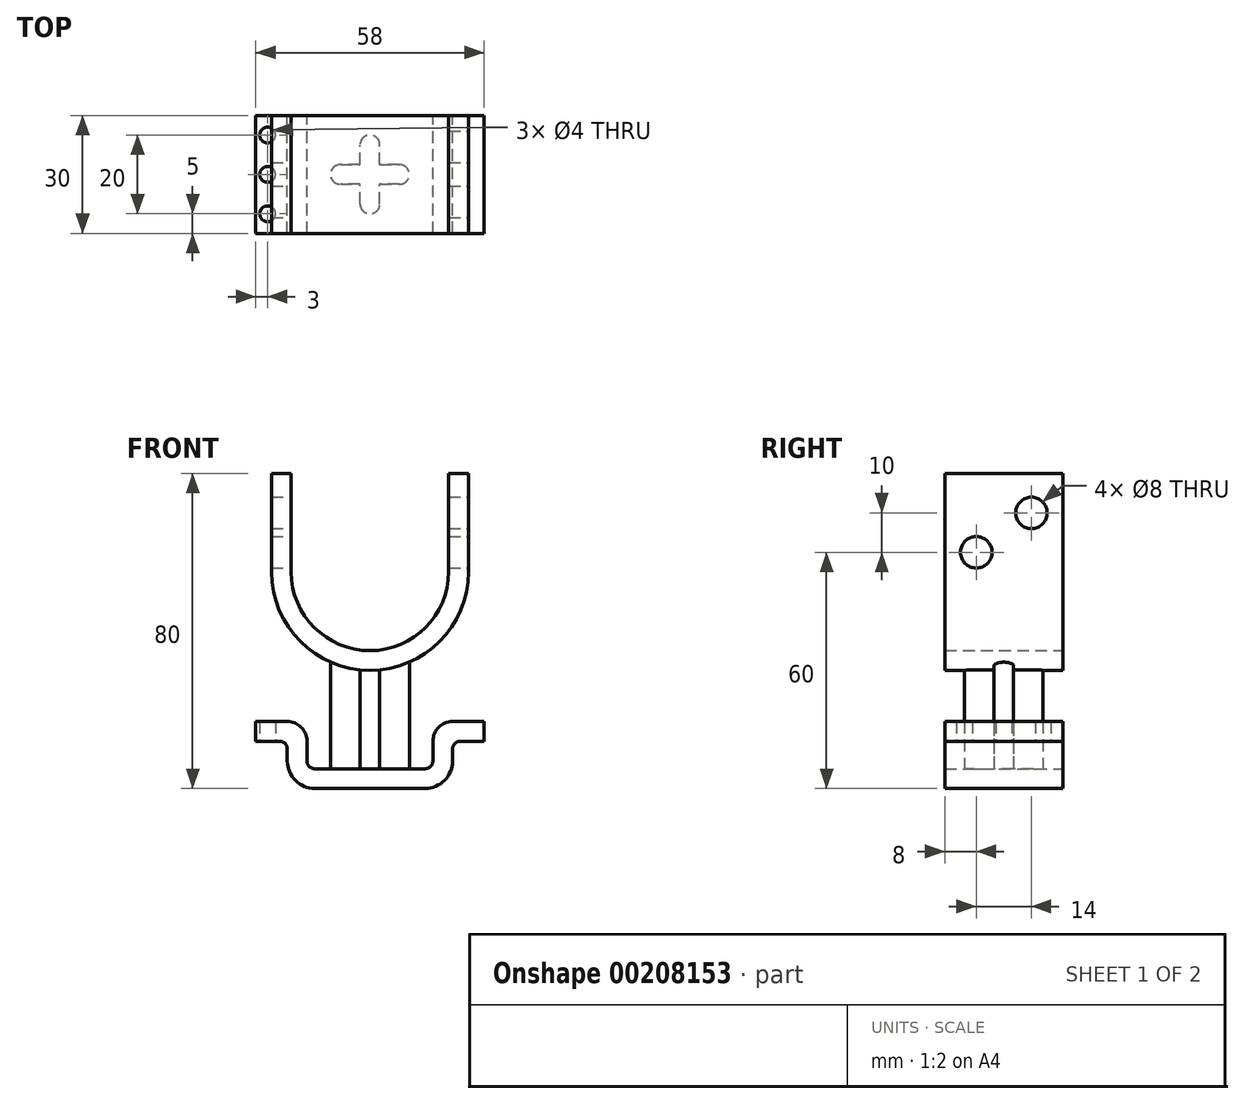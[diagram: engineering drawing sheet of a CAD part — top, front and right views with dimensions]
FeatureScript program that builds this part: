
annotation { "Feature Type Name" : "Feature", "Feature Type Description" : "" }
export const myFeature = defineFeature(function(context is Context, id is Id, definition is map)
    precondition{}
    {
        {
            var Q0;
            Q0=qCreatedBy(makeId("Front.planeOp"),FACE);
            var sketch = newSketch(context, id + "F0", { "sketchPlane" : qUnion([Q0])});
            skArc(sketch, "E0", {"start": v(-25, 0) * mm, "mid": v(0, -25) * mm, "end": v(25, 0) * mm});
            skLineSegment(sketch, "E1", {"start": v(-25, 0) * mm, "end": v(-25, 25) * mm});
            skLineSegment(sketch, "E2", {"start": v(25, 0) * mm, "end": v(25, 25) * mm});
            skLineSegment(sketch, "E3.0", {"start": v(-20, 0) * mm, "end": v(-20, 25) * mm});
            skArc(sketch, "E3.1", {"start": v(-20, 0) * mm, "mid": v(0, -20) * mm, "end": v(20, 0) * mm});
            skLineSegment(sketch, "E3.2", {"start": v(20, 0) * mm, "end": v(20, 25) * mm});
            skLineSegment(sketch, "E4", {"start": v(-25, 25) * mm, "end": v(-20, 25) * mm});
            skLineSegment(sketch, "E5", {"start": v(20, 25) * mm, "end": v(25, 25) * mm});
            skLineSegment(sketch, "E6", {"start": v(0, -50) * mm, "end": v(14, -50) * mm});
            skLineSegment(sketch, "E7", {"start": v(16, -48) * mm, "end": v(16, -43) * mm});
            skLineSegment(sketch, "E8", {"start": v(14, -55) * mm, "end": v(-14, -55) * mm});
            skLineSegment(sketch, "E9", {"start": v(-16, -43) * mm, "end": v(-16, -48) * mm});
            skLineSegment(sketch, "E10", {"start": v(-14, -50) * mm, "end": v(0, -50) * mm});
            skLineSegment(sketch, "E11", {"start": v(-21, -48) * mm, "end": v(-21, -45) * mm});
            skLineSegment(sketch, "E12", {"start": v(-23, -43) * mm, "end": v(-29, -43) * mm});
            skLineSegment(sketch, "E13", {"start": v(-29, -43) * mm, "end": v(-29, -38) * mm});
            skLineSegment(sketch, "E14", {"start": v(-29, -38) * mm, "end": v(-21, -38) * mm});
            skLineSegment(sketch, "E15", {"start": v(21, -48) * mm, "end": v(21, -45) * mm});
            skLineSegment(sketch, "E16", {"start": v(23, -43) * mm, "end": v(29, -43) * mm});
            skLineSegment(sketch, "E17", {"start": v(29, -43) * mm, "end": v(29, -38) * mm});
            skLineSegment(sketch, "E18", {"start": v(29, -38) * mm, "end": v(21, -38) * mm});
            skPoint(sketch, "E19.visualSharp", {"position": v(-16, -38) * mm});
            skArc(sketch, "E19.filletArc", {"start": v(-16, -43) * mm, "mid": v(-17.46, -39.46) * mm, "end": v(-21, -38) * mm});
            skPoint(sketch, "E20.visualSharp", {"position": v(16, -38) * mm});
            skArc(sketch, "E20.filletArc", {"start": v(21, -38) * mm, "mid": v(17.46, -39.46) * mm, "end": v(16, -43) * mm});
            skArc(sketch, "E21.filletArc", {"start": v(-21, -45) * mm, "mid": v(-21.59, -43.59) * mm, "end": v(-23, -43) * mm});
            skArc(sketch, "E22.filletArc", {"start": v(23, -43) * mm, "mid": v(21.59, -43.59) * mm, "end": v(21, -45) * mm});
            skPoint(sketch, "E23.visualSharp", {"position": v(-21, -55) * mm});
            skArc(sketch, "E23.filletArc", {"start": v(-21, -48) * mm, "mid": v(-18.95, -52.95) * mm, "end": v(-14, -55) * mm});
            skPoint(sketch, "E24.visualSharp", {"position": v(21, -55) * mm});
            skArc(sketch, "E24.filletArc", {"start": v(14, -55) * mm, "mid": v(18.95, -52.95) * mm, "end": v(21, -48) * mm});
            skPoint(sketch, "E25.visualSharp", {"position": v(-16, -50) * mm});
            skArc(sketch, "E25.filletArc", {"start": v(-16, -48) * mm, "mid": v(-15.41, -49.41) * mm, "end": v(-14, -50) * mm});
            skPoint(sketch, "E26.visualSharp", {"position": v(16, -50) * mm});
            skArc(sketch, "E26.filletArc", {"start": v(14, -50) * mm, "mid": v(15.41, -49.41) * mm, "end": v(16, -48) * mm});
            skSolve(sketch);
        }
        {
            var Q0;
            Q0=makeQuery(id+"F0.imprint","IMPRINT",FACE,{"disambiguationData":[TD([[makeQuery(id+"F0.imprint","IMPRINT",EDGE,{"derivedFrom":sQuery(id+"F0.wireOp",EDGE,"E0")}),1.0]])]});
            var Q1;
            Q1=makeQuery(id+"F0.imprint","IMPRINT",FACE,{"disambiguationData":[TD([[makeQuery(id+"F0.imprint","IMPRINT",EDGE,{"derivedFrom":sQuery(id+"F0.wireOp",EDGE,"E6")}),-1.0]])]});
            extrude(context, id + "F1", {"entities" : qUnion([Q0, Q1]), "endBound" : BoundingType.SYMMETRIC, "depth" : 30 * mm});
        }
        {
            var Q0;
            Q0=makeQuery(id+"F1.opExtrude","SWEPT_FACE",FACE,{"disambiguationData":[OSD([sQuery(id+"F0.wireOp",EDGE,"E6"),sQuery(id+"F0.wireOp",EDGE,"E10")])]});
            var sketch = newSketch(context, id + "F2", { "sketchPlane" : qUnion([Q0])});
            skLineSegment(sketch, "E27", {"start": v(7.5, 2.5) * mm, "end": v(2.5, 2.5) * mm});
            skLineSegment(sketch, "E28", {"start": v(2.5, 2.5) * mm, "end": v(2.5, 7.5) * mm});
            skLineSegment(sketch, "E29", {"start": v(-2.5, 7.5) * mm, "end": v(-2.5, 2.5) * mm});
            skLineSegment(sketch, "E30", {"start": v(-2.5, 2.5) * mm, "end": v(-7.5, 2.5) * mm});
            skLineSegment(sketch, "E31", {"start": v(-7.5, -2.5) * mm, "end": v(-2.5, -2.5) * mm});
            skLineSegment(sketch, "E32", {"start": v(-2.5, -2.5) * mm, "end": v(-2.5, -7.5) * mm});
            skLineSegment(sketch, "E33", {"start": v(2.5, -7.5) * mm, "end": v(2.5, -2.5) * mm});
            skLineSegment(sketch, "E34", {"start": v(2.5, -2.5) * mm, "end": v(7.5, -2.5) * mm});
            skArc(sketch, "E35", {"start": v(7.5, 2.5) * mm, "mid": v(10, 0) * mm, "end": v(7.5, -2.5) * mm});
            skArc(sketch, "E36", {"start": v(-2.5, 7.5) * mm, "mid": v(0, 10) * mm, "end": v(2.5, 7.5) * mm});
            skArc(sketch, "E37", {"start": v(-7.5, -2.5) * mm, "mid": v(-10, 0) * mm, "end": v(-7.5, 2.5) * mm});
            skArc(sketch, "E38", {"start": v(2.5, -7.5) * mm, "mid": v(0, -10) * mm, "end": v(-2.5, -7.5) * mm});
            skSolve(sketch);
        }
        {
            var Q0;
            Q0=makeQuery(id+"F2.imprint","IMPRINT",FACE,{"disambiguationData":[TD([[makeQuery(id+"F2.imprint","IMPRINT",EDGE,{"derivedFrom":sQuery(id+"F2.wireOp",EDGE,"E27")}),1.0]])]});
            var Q1;
            Q1=makeQuery(id+"F1.opExtrude","SWEPT_FACE",FACE,{"disambiguationData":[OSD([sQuery(id+"F0.wireOp",EDGE,"E0")])]});
            extrude(context, id + "F3", {"entities" : qUnion([Q0]), "operationType" : NewBodyOperationType.ADD, "endBound" : BoundingType.UP_TO_SURFACE, "endBoundEntityFace" : qUnion([Q1]), "depth" : 25 * mm});
        }
        {
            var Q0;
            Q0=makeQuery(id+"F1.opExtrude","SWEPT_FACE",FACE,{"disambiguationData":[OSD([sQuery(id+"F0.wireOp",EDGE,"E12")])]});
            var sketch = newSketch(context, id + "F4", { "sketchPlane" : qUnion([Q0])});
            skCircle(sketch, "E39", {"center": v(-26, 10) * mm, "radius": 2 * mm});
            skCircle(sketch, "E40.1.0.0", {"center": v(-26, 0) * mm, "radius": 2 * mm});
            skCircle(sketch, "E40.2.0.0", {"center": v(-26, -10) * mm, "radius": 2 * mm});
            skLineSegment(sketch, "E40.direction1", {"start": v(-26, 10) * mm, "end": v(-26, 0) * mm, "construction": true});
            skCircle(sketch, "E41.MirrorC", {"center": v(26, 10) * mm, "radius": 2 * mm});
            skCircle(sketch, "E42.MirrorC", {"center": v(26, 0) * mm, "radius": 2 * mm});
            skCircle(sketch, "E43.MirrorC", {"center": v(26, -10) * mm, "radius": 2 * mm});
            skSolve(sketch);
        }
        {
            var Q0;
            Q0=makeQuery(id+"F4.imprint","IMPRINT",FACE,{"disambiguationData":[TD([[makeQuery(id+"F4.imprint","IMPRINT",EDGE,{"derivedFrom":sQuery(id+"F4.wireOp",EDGE,"E40.2.0.0")}),1.0]])]});
            var Q1;
            Q1=makeQuery(id+"F4.imprint","IMPRINT",FACE,{"disambiguationData":[TD([[makeQuery(id+"F4.imprint","IMPRINT",EDGE,{"derivedFrom":sQuery(id+"F4.wireOp",EDGE,"E40.1.0.0")}),1.0]])]});
            var Q2;
            Q2=makeQuery(id+"F4.imprint","IMPRINT",FACE,{"disambiguationData":[TD([[makeQuery(id+"F4.imprint","IMPRINT",EDGE,{"derivedFrom":sQuery(id+"F4.wireOp",EDGE,"E39")}),1.0]])]});
            var Q3;
            Q3=makeQuery(id+"F4.imprint","IMPRINT",FACE,{"disambiguationData":[TD([[makeQuery(id+"F4.imprint","IMPRINT",EDGE,{"derivedFrom":sQuery(id+"F4.wireOp",EDGE,"E43.MirrorC")}),-1.0]])]});
            var Q4;
            Q4=makeQuery(id+"F4.imprint","IMPRINT",FACE,{"disambiguationData":[TD([[makeQuery(id+"F4.imprint","IMPRINT",EDGE,{"derivedFrom":sQuery(id+"F4.wireOp",EDGE,"E42.MirrorC")}),-1.0]])]});
            var Q5;
            Q5=makeQuery(id+"F4.imprint","IMPRINT",FACE,{"disambiguationData":[TD([[makeQuery(id+"F4.imprint","IMPRINT",EDGE,{"derivedFrom":sQuery(id+"F4.wireOp",EDGE,"E41.MirrorC")}),-1.0]])]});
            extrude(context, id + "F5", {"entities" : qUnion([Q0, Q1, Q2, Q3, Q4, Q5]), "operationType" : NewBodyOperationType.REMOVE, "endBound" : BoundingType.UP_TO_NEXT, "oppositeDirection" : true, "depth" : 25 * mm});
        }
        {
            var Q0;
            Q0=makeQuery(id+"F1.opExtrude","SWEPT_FACE",FACE,{"disambiguationData":[OSD([sQuery(id+"F0.wireOp",EDGE,"E2")])]});
            var sketch = newSketch(context, id + "F6", { "sketchPlane" : qUnion([Q0])});
            skCircle(sketch, "E44", {"center": v(-7, 5) * mm, "radius": 4 * mm});
            skCircle(sketch, "E45", {"center": v(7, 15) * mm, "radius": 4 * mm});
            skSolve(sketch);
        }
        {
            var Q0;
            Q0=makeQuery(id+"F6.imprint","IMPRINT",FACE,{"disambiguationData":[TD([[makeQuery(id+"F6.imprint","IMPRINT",EDGE,{"derivedFrom":sQuery(id+"F6.wireOp",EDGE,"E44")}),1.0]])]});
            var Q1;
            Q1=makeQuery(id+"F6.imprint","IMPRINT",FACE,{"disambiguationData":[TD([[makeQuery(id+"F6.imprint","IMPRINT",EDGE,{"derivedFrom":sQuery(id+"F6.wireOp",EDGE,"E45")}),1.0]])]});
            extrude(context, id + "F7", {"entities" : qUnion([Q0, Q1]), "operationType" : NewBodyOperationType.REMOVE, "endBound" : BoundingType.THROUGH_ALL, "oppositeDirection" : true, "depth" : 25 * mm});
        }
    });
